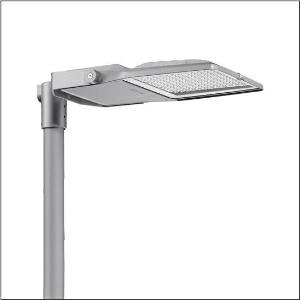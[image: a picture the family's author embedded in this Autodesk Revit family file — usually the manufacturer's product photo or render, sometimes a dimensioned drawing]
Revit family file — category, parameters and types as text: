
# Revit family: floodlight_fl_21_iq_midi___pl52_5xa7782e4d3a_8c54
name_source: partatom
category: Lighting Fixtures
units: mm (PartAtom-declared; Revit-internal decimal feet)

## family parameters
Cut with Voids When Loaded = No
Host = Face
Light Source = No
Part Type = Normal
Room Calculation Point = No
Round Connector Dimension = Use Diameter
Shared = No

## types (1)
- --- (1 x LED, 28010 lm, 208.1 W, 4000K)
    Apparent Load = 208 VA
    CIE Flux Codes = 26 60 98 100 100
    Color Rendering = 70
    Color Temperature = 4000K
    Default Elevation = 1800 mm
    Description = Floodlight FL 21 iQ midi, floodlight, primary light control with lens, of PMMA, primary optical cover: protective disc, of toughened safety glass, transparent, light distribution: PL52, light emission: direct distribution, installation type: surface-mounted, LED, High Power LED, rated luminous flux: 28.010lm, luminous efficacy: 135lm/W, light colour: 740, colour temperature: 4000K, control gear: ECG iQ, control: optimised constant luminous flux control (CLO 2.0), Desk-Remote (wireless, voltage-free reading and setting of iQ features in the workshop via application-optimized NFC function/RFID function), Smart-Wire, Night-Set, Temp-Guard, Auto-Match, Street-Remote, with terminal, 6-pole, mains connection: 220..240V, AC, 50/60Hz, start of lifetime: 208W, end of service life: 227W, reduction: 90W, luminaire housing, of diecast aluminium, powder-coated, Siteco® metallic grey (DB 702S), corrosivity category C5 mid according to DIN EN ISO 12944, sealing non-destructively replaceable, please order mast flange separately, mast bracket, of steel, galvanised, powder-coated, Siteco® metallic grey (DB 702S), protection rating (complete): IP66, insulation class (complete): insulation class II (safety insulation), certification: CE, protection symbol: D, impact resistance: IK08, permissible operating ambient temperature: -40..+40°C, permissible operating ambient temperature for outdoor applications: -40..+50°C, standard: DIN EN 12944, LABS conformity tested according to VDMA 24364:2018-05, packaging unit: 1 piece

Light Distribution: PL52
    Height = 76 mm
    Lamp = 1 x LED
    Lamp Light Flux = 28010 lm
    Lamp Power = 208.1 W
    Lamp count = 1
    Length = 657 mm
    Luminous efficacy = 135 lm/W
    Manufacturer = Siteco
    ModVariant = No
    Model = 5XA7782E4D3A
    Number of Poles = 1
    OnlyDefault = Yes
    Power Factor = 1
    Product Name = Floodlight FL 21 iQ midi | PL52
    Product group = floodlight | pylon annexe
    ProductGroupID = 6200
    Protection Class = Protection class II
    Protection Degree = IP 66
    RLX_Detail_Level = 1
    RLX_Emergency_Light_Flux = 0 lm
    RLX_Emergency_Type = 0
    RLX_Emergency_Type_DB = No
    RlxData = <blob elided: 153873 chars, md5=2e541f7d>
    Socket = socket
    Standby Power = 0 W
    System Light Flux = 28010 lm
    System Power = 208 W
    Type Comments = factory setting: luminous flux: 100 % | dim-lin: 254 | 710 mA
    Type Image = l_1007123.jpg
    URL = http://relux.com
    VarID = @adj_054257
    Voltage = 0 V
    Weight = 0.00 kg
    Width = 442 mm

## geometry (parser evidence)
native form markers: Blend x4, Sweep x13
no freeform markers — native parametric forms only
